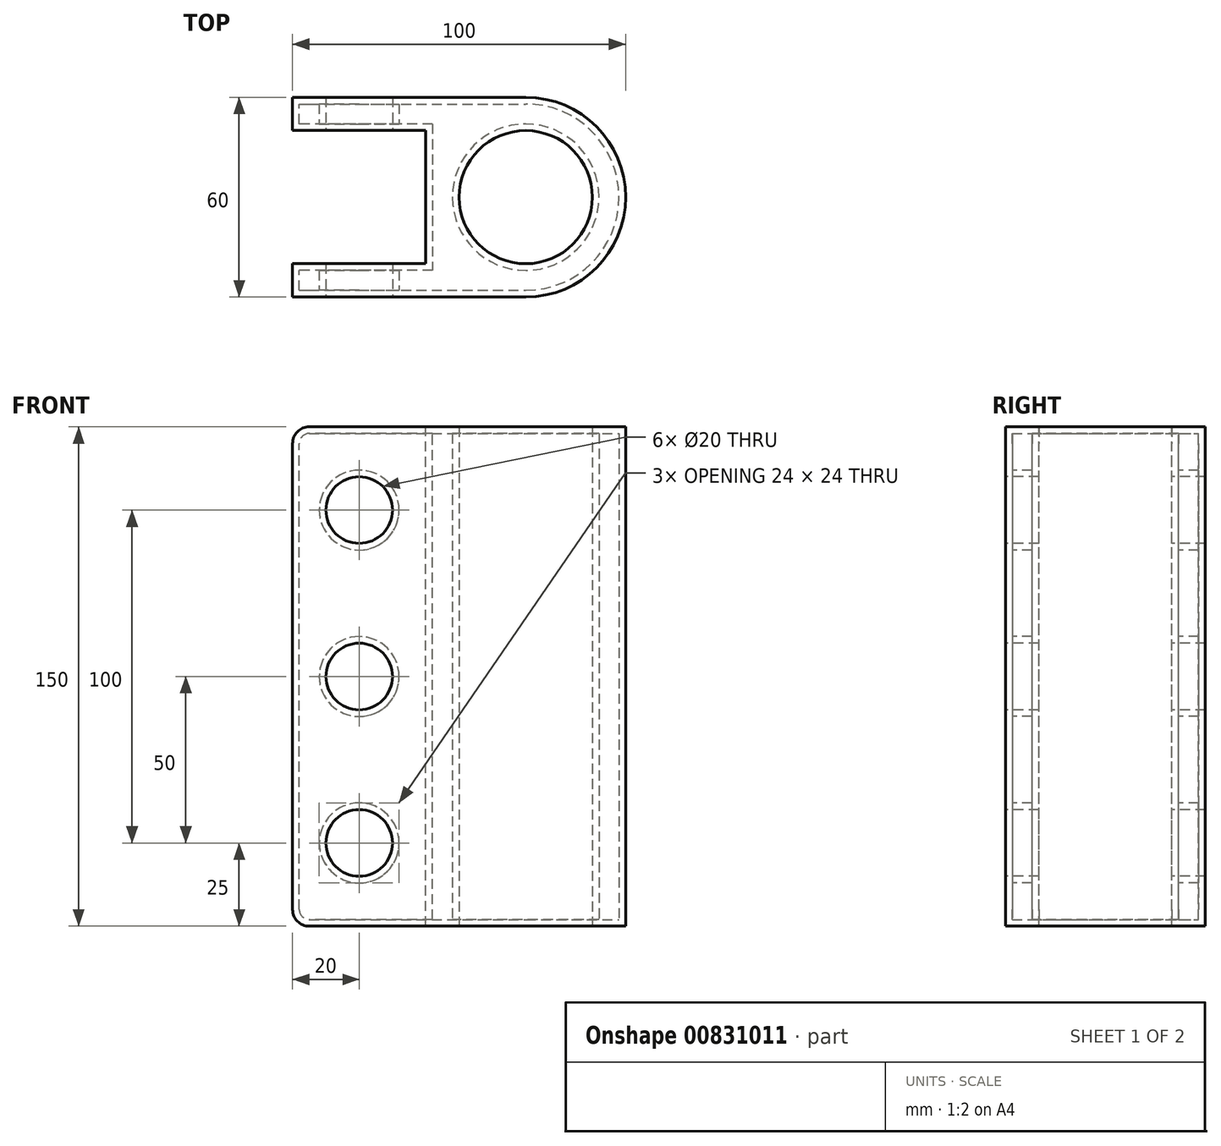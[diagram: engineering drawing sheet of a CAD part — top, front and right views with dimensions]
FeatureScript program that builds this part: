
annotation { "Feature Type Name" : "Feature", "Feature Type Description" : "" }
export const myFeature = defineFeature(function(context is Context, id is Id, definition is map)
    precondition{}
    {
        {
            var Q0;
            Q0=qCreatedBy(makeId("Top.planeOp"),FACE);
            var sketch = newSketch(context, id + "F0", { "sketchPlane" : qUnion([Q0])});
            skCircle(sketch, "E0", {"center": v(0, 0) * mm, "radius": 20 * mm});
            skLineSegment(sketch, "E1.bottom", {"start": v(-70, 30) * mm, "end": v(0, 30) * mm});
            skLineSegment(sketch, "E1.top", {"start": v(-70, -30) * mm, "end": v(0, -30) * mm});
            skLineSegment(sketch, "E1.left", {"start": v(-70, 30) * mm, "end": v(-70, -30) * mm});
            skCircle(sketch, "E2", {"center": v(0, 0) * mm, "radius": 30 * mm});
            skSolve(sketch);
        }
        {
            var Q0;
            Q0=makeQuery(id+"F0.imprint","IMPRINT",FACE,{"disambiguationData":[TD([[makeQuery(id+"F0.imprint","IMPRINT",EDGE,{"derivedFrom":sQuery(id+"F0.wireOp",EDGE,"E0")}),-1.0]])]});
            var Q1;
            {var subQ0=sQuery(id+"F0.wireOp",EDGE,"E1.bottom");Q1=makeQuery(id+"F0.imprint","IMPRINT",FACE,{"disambiguationData":[TD([[makeQuery(id+"F0.imprint","IMPRINT",EDGE,{"derivedFrom":subQ0}),-1.0]])]});}
            extrude(context, id + "F1", {"entities" : qUnion([Q0, Q1]), "endBound" : BoundingType.SYMMETRIC, "depth" : 150 * mm, "offsetDistance" : 25 * mm});
        }
        {
            var Q0;
            Q0=makeQuery(id+"F1.opExtrude","SWEPT_FACE",FACE,{"disambiguationData":[OSD([sQuery(id+"F0.wireOp",EDGE,"E1.left")])]});
            var sketch = newSketch(context, id + "F2", { "sketchPlane" : qUnion([Q0])});
            skLineSegment(sketch, "E3.bottom", {"start": v(-20, -75) * mm, "end": v(20, -75) * mm});
            skLineSegment(sketch, "E3.top", {"start": v(-20, 75) * mm, "end": v(20, 75) * mm});
            skLineSegment(sketch, "E3.left", {"start": v(-20, -75) * mm, "end": v(-20, 75) * mm});
            skLineSegment(sketch, "E3.right", {"start": v(20, -75) * mm, "end": v(20, 75) * mm});
            skSolve(sketch);
        }
        {
            var Q0;
            Q0=makeQuery(id+"F2.imprint","IMPRINT",FACE,{"disambiguationData":[TD([[makeQuery(id+"F2.imprint","IMPRINT",EDGE,{"derivedFrom":sQuery(id+"F2.wireOp",EDGE,"E3.bottom")}),1.0]])]});
            extrude(context, id + "F3", {"entities" : qUnion([Q0]), "operationType" : NewBodyOperationType.REMOVE, "oppositeDirection" : true, "depth" : 40 * mm, "offsetDistance" : 25 * mm});
        }
        {
            var Q0;
            Q0=makeQuery(id+"F1.opExtrude","SWEPT_FACE",FACE,{"disambiguationData":[OSD([sQuery(id+"F0.wireOp",EDGE,"E1.top")])]});
            var sketch = newSketch(context, id + "F4", { "sketchPlane" : qUnion([Q0])});
            skCircle(sketch, "E4", {"center": v(-50, 50) * mm, "radius": 10 * mm});
            skCircle(sketch, "E5", {"center": v(-50, -50) * mm, "radius": 10 * mm});
            skCircle(sketch, "E6", {"center": v(-50, 0) * mm, "radius": 10 * mm});
            skSolve(sketch);
        }
        {
            var Q0;
            Q0=makeQuery(id+"F4.imprint","IMPRINT",FACE,{"disambiguationData":[TD([[makeQuery(id+"F4.imprint","IMPRINT",EDGE,{"derivedFrom":sQuery(id+"F4.wireOp",EDGE,"E4")}),1.0]])]});
            var Q1;
            Q1=makeQuery(id+"F4.imprint","IMPRINT",FACE,{"disambiguationData":[TD([[makeQuery(id+"F4.imprint","IMPRINT",EDGE,{"derivedFrom":sQuery(id+"F4.wireOp",EDGE,"E6")}),1.0]])]});
            var Q2;
            Q2=makeQuery(id+"F4.imprint","IMPRINT",FACE,{"disambiguationData":[TD([[makeQuery(id+"F4.imprint","IMPRINT",EDGE,{"derivedFrom":sQuery(id+"F4.wireOp",EDGE,"E5")}),1.0]])]});
            extrude(context, id + "F5", {"entities" : qUnion([Q0, Q1, Q2]), "operationType" : NewBodyOperationType.REMOVE, "oppositeDirection" : true, "depth" : 60 * mm, "offsetDistance" : 25 * mm});
        }
        {
            var Q0;
            {var subQ0=sQuery(id+"F0.wireOp",EDGE,"E1.left");var subQ1=sQuery(id+"F0.wireOp",EDGE,"E1.bottom");Q0=makeQuery(id+"F3.boolean.opBoolean","SPLIT",EDGE,{"disambiguationData":[TD([makeQuery(id+"F1.opExtrude","SWEPT_FACE",FACE,{"disambiguationData":[OSD([subQ1])]})])],"derivedFrom":makeQuery(id+"F1.opExtrude","CAP_EDGE",EDGE,{"disambiguationData":[OSD([subQ0])],"isStart":false})});}
            var Q1;
            {var subQ0=sQuery(id+"F0.wireOp",EDGE,"E1.left");var subQ1=sQuery(id+"F0.wireOp",EDGE,"E1.top");Q1=makeQuery(id+"F3.boolean.opBoolean","SPLIT",EDGE,{"disambiguationData":[TD([makeQuery(id+"F1.opExtrude","SWEPT_FACE",FACE,{"disambiguationData":[OSD([subQ1])]})])],"derivedFrom":makeQuery(id+"F1.opExtrude","CAP_EDGE",EDGE,{"disambiguationData":[OSD([subQ0])],"isStart":false})});}
            var Q2;
            {var subQ0=sQuery(id+"F0.wireOp",EDGE,"E1.left");var subQ1=sQuery(id+"F0.wireOp",EDGE,"E1.bottom");Q2=makeQuery(id+"F3.boolean.opBoolean","SPLIT",EDGE,{"disambiguationData":[TD([makeQuery(id+"F1.opExtrude","SWEPT_FACE",FACE,{"disambiguationData":[OSD([subQ1])]})])],"derivedFrom":makeQuery(id+"F1.opExtrude","CAP_EDGE",EDGE,{"disambiguationData":[OSD([subQ0])],"isStart":true})});}
            var Q3;
            {var subQ0=sQuery(id+"F0.wireOp",EDGE,"E1.left");var subQ1=sQuery(id+"F0.wireOp",EDGE,"E1.top");Q3=makeQuery(id+"F3.boolean.opBoolean","SPLIT",EDGE,{"disambiguationData":[TD([makeQuery(id+"F1.opExtrude","SWEPT_FACE",FACE,{"disambiguationData":[OSD([subQ1])]})])],"derivedFrom":makeQuery(id+"F1.opExtrude","CAP_EDGE",EDGE,{"disambiguationData":[OSD([subQ0])],"isStart":true})});}
            fillet(context, id + "F6", {"entities" : qUnion([Q0, Q1, Q2, Q3]), "radius" : 5 * mm, "tangentPropagation" : true, "allowEdgeOverflow" : false});
        }
        {
            var Q0;
            Q0=makeQuery(id+"F1.opExtrude","SWEPT_FACE",FACE,{"disambiguationData":[OSD([sQuery(id+"F0.wireOp",EDGE,"E0")])]});
            var Q1;
            Q1=makeQuery(id+"F1.opExtrude","SWEPT_FACE",FACE,{"disambiguationData":[OSD([sQuery(id+"F0.wireOp",EDGE,"E2")])]});
            var Q2;
            Q2=makeQuery(id+"F3.boolean.opBoolean","COPY",FACE,{"derivedFrom":makeQuery(id+"F3.opExtrude","CAP_FACE",FACE,{"disambiguationData":[OSD([sQuery(id+"F2.wireOp",EDGE,"E3.bottom"),sQuery(id+"F2.wireOp",EDGE,"E3.top"),sQuery(id+"F2.wireOp",EDGE,"E3.left"),sQuery(id+"F2.wireOp",EDGE,"E3.right")])],"isStart":false})});
            var Q3;
            Q3=makeQuery(id+"F5.boolean.opBoolean","COPY",FACE,{"disambiguationData":[TD([makeQuery(id+"F1.opExtrude","SWEPT_FACE",FACE,{"disambiguationData":[OSD([sQuery(id+"F0.wireOp",EDGE,"E1.top")])]})])],"derivedFrom":makeQuery(id+"F5.opExtrude","SWEPT_FACE",FACE,{"disambiguationData":[OSD([sQuery(id+"F4.wireOp",EDGE,"E4")])]})});
            var Q4;
            Q4=makeQuery(id+"F5.boolean.opBoolean","COPY",FACE,{"disambiguationData":[TD([makeQuery(id+"F1.opExtrude","SWEPT_FACE",FACE,{"disambiguationData":[OSD([sQuery(id+"F0.wireOp",EDGE,"E1.bottom")])]})])],"derivedFrom":makeQuery(id+"F5.opExtrude","SWEPT_FACE",FACE,{"disambiguationData":[OSD([sQuery(id+"F4.wireOp",EDGE,"E4")])]})});
            var Q5;
            Q5=makeQuery(id+"F5.boolean.opBoolean","COPY",FACE,{"disambiguationData":[TD([makeQuery(id+"F1.opExtrude","SWEPT_FACE",FACE,{"disambiguationData":[OSD([sQuery(id+"F0.wireOp",EDGE,"E1.top")])]})])],"derivedFrom":makeQuery(id+"F5.opExtrude","SWEPT_FACE",FACE,{"disambiguationData":[OSD([sQuery(id+"F4.wireOp",EDGE,"E5")])]})});
            var Q6;
            Q6=makeQuery(id+"F5.boolean.opBoolean","COPY",FACE,{"disambiguationData":[TD([makeQuery(id+"F1.opExtrude","SWEPT_FACE",FACE,{"disambiguationData":[OSD([sQuery(id+"F0.wireOp",EDGE,"E1.top")])]})])],"derivedFrom":makeQuery(id+"F5.opExtrude","SWEPT_FACE",FACE,{"disambiguationData":[OSD([sQuery(id+"F4.wireOp",EDGE,"E6")])]})});
            var Q7;
            {var subQ0=sQuery(id+"F0.wireOp",EDGE,"E1.left");var subQ1=sQuery(id+"F0.wireOp",EDGE,"E1.top");Q7=makeQuery(id+"F6.opFillet","BLEND_FACE",FACE,{"disambiguationData":[OSD([subQ0]),TDD([makeQuery(id+"F3.boolean.opBoolean","SPLIT",EDGE,{"disambiguationData":[TD([makeQuery(id+"F1.opExtrude","SWEPT_FACE",FACE,{"disambiguationData":[OSD([subQ1])]})])],"derivedFrom":makeQuery(id+"F1.opExtrude","CAP_EDGE",EDGE,{"disambiguationData":[OSD([subQ0])],"isStart":true})})])]});}
            var Q8;
            {var subQ0=sQuery(id+"F0.wireOp",EDGE,"E1.left");var subQ1=sQuery(id+"F0.wireOp",EDGE,"E1.bottom");Q8=makeQuery(id+"F6.opFillet","BLEND_FACE",FACE,{"disambiguationData":[OSD([subQ0]),TDD([makeQuery(id+"F3.boolean.opBoolean","SPLIT",EDGE,{"disambiguationData":[TD([makeQuery(id+"F1.opExtrude","SWEPT_FACE",FACE,{"disambiguationData":[OSD([subQ1])]})])],"derivedFrom":makeQuery(id+"F1.opExtrude","CAP_EDGE",EDGE,{"disambiguationData":[OSD([subQ0])],"isStart":false})})])]});}
            var Q9;
            {var subQ0=sQuery(id+"F0.wireOp",EDGE,"E1.left");var subQ1=sQuery(id+"F0.wireOp",EDGE,"E1.top");Q9=makeQuery(id+"F6.opFillet","BLEND_FACE",FACE,{"disambiguationData":[OSD([subQ0]),TDD([makeQuery(id+"F3.boolean.opBoolean","SPLIT",EDGE,{"disambiguationData":[TD([makeQuery(id+"F1.opExtrude","SWEPT_FACE",FACE,{"disambiguationData":[OSD([subQ1])]})])],"derivedFrom":makeQuery(id+"F1.opExtrude","CAP_EDGE",EDGE,{"disambiguationData":[OSD([subQ0])],"isStart":false})})])]});}
            var Q10;
            Q10=makeQuery(id+"F1.opExtrude","CAP_FACE",FACE,{"disambiguationData":[OSD([sQuery(id+"F0.wireOp",EDGE,"E0"),sQuery(id+"F0.wireOp",EDGE,"E1.bottom"),sQuery(id+"F0.wireOp",EDGE,"E1.top"),sQuery(id+"F0.wireOp",EDGE,"E1.left"),sQuery(id+"F0.wireOp",EDGE,"E2")])],"isStart":false});
            var Q11;
            {var subQ1=sQuery(id+"F0.wireOp",EDGE,"E1.left");var subQ3=sQuery(id+"F0.wireOp",EDGE,"E1.bottom");Q11=makeQuery(id+"F3.boolean.opBoolean","SPLIT",FACE,{"disambiguationData":[TD([makeQuery(id+"F1.opExtrude","SWEPT_FACE",FACE,{"disambiguationData":[OSD([subQ3])]})])],"derivedFrom":makeQuery(id+"F1.opExtrude","SWEPT_FACE",FACE,{"disambiguationData":[OSD([subQ1])]})});}
            var Q12;
            {var subQ1=sQuery(id+"F0.wireOp",EDGE,"E1.left");var subQ2=sQuery(id+"F0.wireOp",EDGE,"E1.top");Q12=makeQuery(id+"F3.boolean.opBoolean","SPLIT",FACE,{"disambiguationData":[TD([makeQuery(id+"F1.opExtrude","SWEPT_FACE",FACE,{"disambiguationData":[OSD([subQ2])]})])],"derivedFrom":makeQuery(id+"F1.opExtrude","SWEPT_FACE",FACE,{"disambiguationData":[OSD([subQ1])]})});}
            var Q13;
            Q13=makeQuery(id+"F1.opExtrude","SWEPT_FACE",FACE,{"disambiguationData":[OSD([sQuery(id+"F0.wireOp",EDGE,"E1.top")])]});
            var Q14;
            Q14=makeQuery(id+"F3.boolean.opBoolean","COPY",FACE,{"derivedFrom":makeQuery(id+"F3.opExtrude","SWEPT_FACE",FACE,{"disambiguationData":[OSD([sQuery(id+"F2.wireOp",EDGE,"E3.left")])]})});
            var Q15;
            Q15=makeQuery(id+"F3.boolean.opBoolean","COPY",FACE,{"derivedFrom":makeQuery(id+"F3.opExtrude","SWEPT_FACE",FACE,{"disambiguationData":[OSD([sQuery(id+"F2.wireOp",EDGE,"E3.right")])]})});
            var Q16;
            Q16=makeQuery(id+"F5.boolean.opBoolean","COPY",FACE,{"disambiguationData":[TD([makeQuery(id+"F1.opExtrude","SWEPT_FACE",FACE,{"disambiguationData":[OSD([sQuery(id+"F0.wireOp",EDGE,"E1.bottom")])]})])],"derivedFrom":makeQuery(id+"F5.opExtrude","SWEPT_FACE",FACE,{"disambiguationData":[OSD([sQuery(id+"F4.wireOp",EDGE,"E5")])]})});
            var Q17;
            Q17=makeQuery(id+"F5.boolean.opBoolean","COPY",FACE,{"disambiguationData":[TD([makeQuery(id+"F1.opExtrude","SWEPT_FACE",FACE,{"disambiguationData":[OSD([sQuery(id+"F0.wireOp",EDGE,"E1.bottom")])]})])],"derivedFrom":makeQuery(id+"F5.opExtrude","SWEPT_FACE",FACE,{"disambiguationData":[OSD([sQuery(id+"F4.wireOp",EDGE,"E6")])]})});
            var Q18;
            {var subQ0=sQuery(id+"F0.wireOp",EDGE,"E1.left");var subQ1=sQuery(id+"F0.wireOp",EDGE,"E1.bottom");Q18=makeQuery(id+"F6.opFillet","BLEND_FACE",FACE,{"disambiguationData":[OSD([subQ0]),TDD([makeQuery(id+"F3.boolean.opBoolean","SPLIT",EDGE,{"disambiguationData":[TD([makeQuery(id+"F1.opExtrude","SWEPT_FACE",FACE,{"disambiguationData":[OSD([subQ1])]})])],"derivedFrom":makeQuery(id+"F1.opExtrude","CAP_EDGE",EDGE,{"disambiguationData":[OSD([subQ0])],"isStart":true})})])]});}
            var Q19;
            Q19=makeQuery(id+"F1.opExtrude","CAP_FACE",FACE,{"disambiguationData":[OSD([sQuery(id+"F0.wireOp",EDGE,"E0"),sQuery(id+"F0.wireOp",EDGE,"E1.bottom"),sQuery(id+"F0.wireOp",EDGE,"E1.top"),sQuery(id+"F0.wireOp",EDGE,"E1.left"),sQuery(id+"F0.wireOp",EDGE,"E2")])],"isStart":true});
            var Q20;
            Q20=makeQuery(id+"F1.opExtrude","SWEPT_FACE",FACE,{"disambiguationData":[OSD([sQuery(id+"F0.wireOp",EDGE,"E1.bottom")])]});
            var Q21;
            Q21=makeQuery(id+"F1.opExtrude","SWEPT_BODY",BODY,{"disambiguationData":[OSD([sQuery(id+"F0.wireOp",EDGE,"E0"),sQuery(id+"F0.wireOp",EDGE,"E1.bottom"),sQuery(id+"F0.wireOp",EDGE,"E1.top"),sQuery(id+"F0.wireOp",EDGE,"E1.left"),sQuery(id+"F0.wireOp",EDGE,"E2")])]});
            shell(context, id + "F7", {"isHollow" : true, "entities" : qUnion([Q0, Q1, Q2, Q3, Q4, Q5, Q6, Q7, Q8, Q9, Q10, Q11, Q12, Q13, Q14, Q15, Q16, Q17, Q18, Q19, Q20]), "parts" : qUnion([Q21]), "thickness" : 2 * mm});
        }
    });
